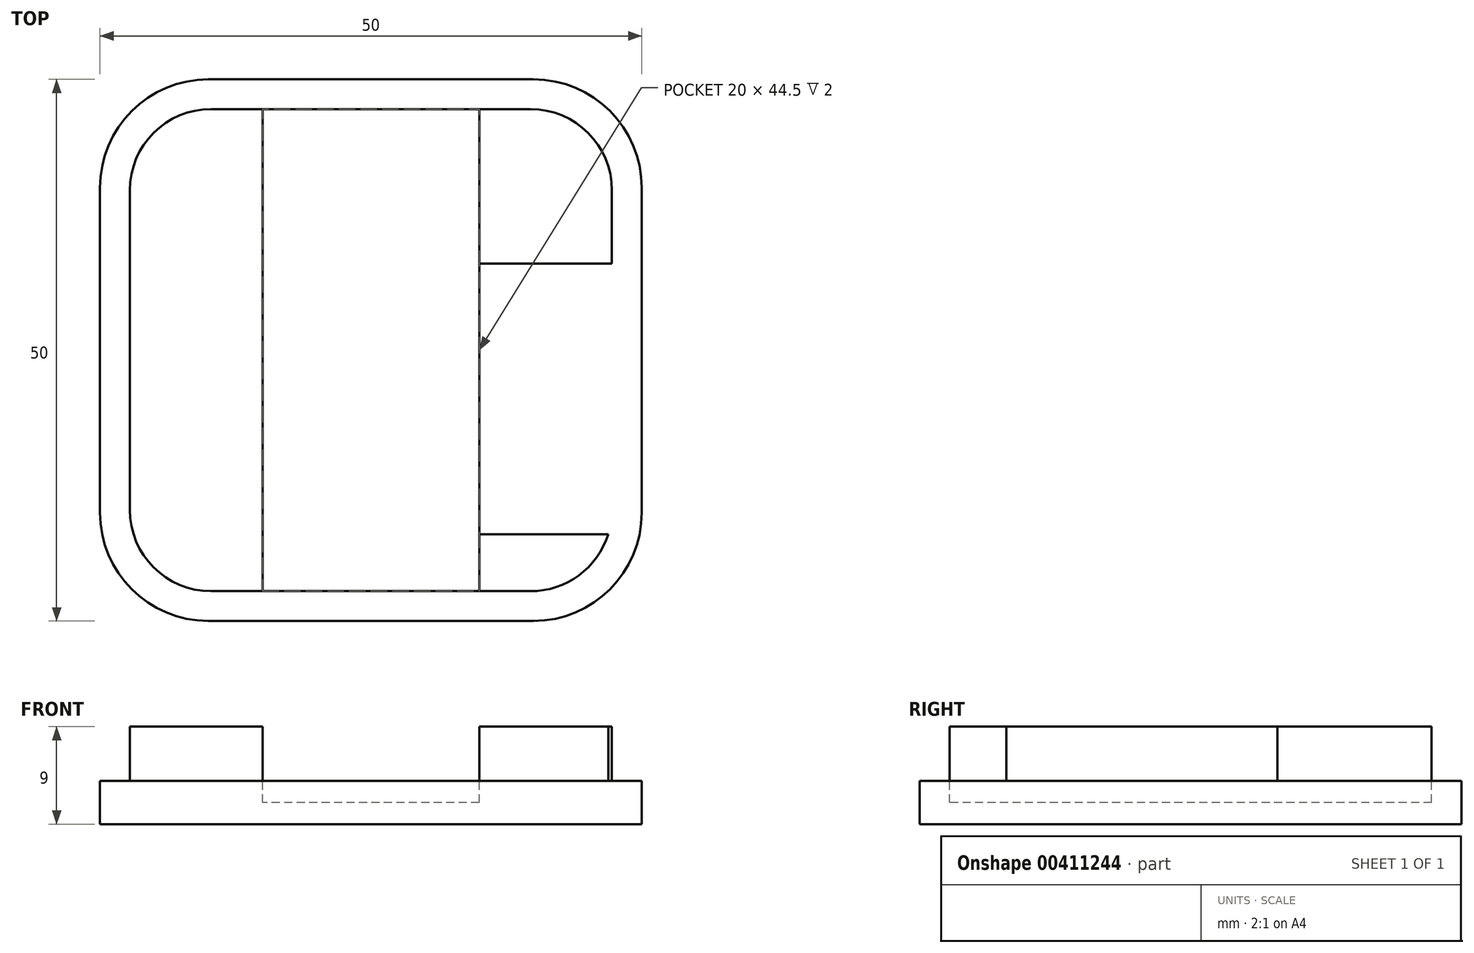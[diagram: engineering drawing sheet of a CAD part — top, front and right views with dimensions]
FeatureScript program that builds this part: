
annotation { "Feature Type Name" : "Feature", "Feature Type Description" : "" }
export const myFeature = defineFeature(function(context is Context, id is Id, definition is map)
    precondition{}
    {
        {
            var Q0;
            Q0=qCreatedBy(makeId("Top.planeOp"),FACE);
            var sketch = newSketch(context, id + "F0", { "sketchPlane" : qUnion([Q0])});
            skLineSegment(sketch, "E0.bottom", {"start": v(15, 25) * mm, "end": v(-15, 25) * mm});
            skLineSegment(sketch, "E0.top", {"start": v(15, -25) * mm, "end": v(-15, -25) * mm});
            skLineSegment(sketch, "E0.left", {"start": v(25, 15) * mm, "end": v(25, -15) * mm});
            skLineSegment(sketch, "E0.right", {"start": v(-25, 15) * mm, "end": v(-25, -15) * mm});
            skPoint(sketch, "E0.middle", {"position": v(0, 0) * mm});
            skPoint(sketch, "E1.visualSharp", {"position": v(-25, 25) * mm});
            skArc(sketch, "E1.filletArc", {"start": v(-15, 25) * mm, "mid": v(-22.07, 22.07) * mm, "end": v(-25, 15) * mm});
            skPoint(sketch, "E2.visualSharp", {"position": v(25, 25) * mm});
            skArc(sketch, "E2.filletArc", {"start": v(25, 15) * mm, "mid": v(22.07, 22.07) * mm, "end": v(15, 25) * mm});
            skPoint(sketch, "E3.visualSharp", {"position": v(25, -25) * mm});
            skArc(sketch, "E3.filletArc", {"start": v(15, -25) * mm, "mid": v(22.07, -22.07) * mm, "end": v(25, -15) * mm});
            skPoint(sketch, "E4.visualSharp", {"position": v(-25, -25) * mm});
            skArc(sketch, "E4.filletArc", {"start": v(-25, -15) * mm, "mid": v(-22.07, -22.07) * mm, "end": v(-15, -25) * mm});
            skSolve(sketch);
        }
        {
            var Q0;
            Q0=makeQuery(id+"F0.imprint","IMPRINT",FACE,{"disambiguationData":[TD([[makeQuery(id+"F0.imprint","IMPRINT",EDGE,{"derivedFrom":sQuery(id+"F0.wireOp",EDGE,"E0.bottom")}),1.0]])]});
            extrude(context, id + "F1", {"entities" : qUnion([Q0]), "depth" : 4 * mm});
        }
        {
            var Q0;
            Q0=makeQuery(id+"F1.opExtrude","CAP_FACE",FACE,{"disambiguationData":[OSD([sQuery(id+"F0.wireOp",EDGE,"E0.bottom"),sQuery(id+"F0.wireOp",EDGE,"E0.top"),sQuery(id+"F0.wireOp",EDGE,"E0.left"),sQuery(id+"F0.wireOp",EDGE,"E0.right"),sQuery(id+"F0.wireOp",EDGE,"E1.filletArc"),sQuery(id+"F0.wireOp",EDGE,"E2.filletArc"),sQuery(id+"F0.wireOp",EDGE,"E3.filletArc"),sQuery(id+"F0.wireOp",EDGE,"E4.filletArc")])],"isStart":false});
            var sketch = newSketch(context, id + "F2", { "sketchPlane" : qUnion([Q0])});
            skLineSegment(sketch, "E5.bottom", {"start": v(14.75, 22.25) * mm, "end": v(-14.75, 22.25) * mm});
            skLineSegment(sketch, "E5.top", {"start": v(14.75, -22.25) * mm, "end": v(-14.75, -22.25) * mm});
            skLineSegment(sketch, "E5.left", {"start": v(22.25, 14.75) * mm, "end": v(22.25, -14.75) * mm});
            skLineSegment(sketch, "E5.right", {"start": v(-22.25, 14.75) * mm, "end": v(-22.25, -14.75) * mm});
            skPoint(sketch, "E5.middle", {"position": v(0, 0) * mm});
            skPoint(sketch, "E6.visualSharp", {"position": v(-22.25, 22.25) * mm});
            skArc(sketch, "E6.filletArc", {"start": v(-14.75, 22.25) * mm, "mid": v(-20.05, 20.05) * mm, "end": v(-22.25, 14.75) * mm});
            skPoint(sketch, "E7.visualSharp", {"position": v(22.25, 22.25) * mm});
            skArc(sketch, "E7.filletArc", {"start": v(22.25, 14.75) * mm, "mid": v(20.05, 20.05) * mm, "end": v(14.75, 22.25) * mm});
            skPoint(sketch, "E8.visualSharp", {"position": v(22.25, -22.25) * mm});
            skArc(sketch, "E8.filletArc", {"start": v(14.75, -22.25) * mm, "mid": v(20.05, -20.05) * mm, "end": v(22.25, -14.75) * mm});
            skPoint(sketch, "E9.visualSharp", {"position": v(-22.25, -22.25) * mm});
            skArc(sketch, "E9.filletArc", {"start": v(-22.25, -14.75) * mm, "mid": v(-20.05, -20.05) * mm, "end": v(-14.75, -22.25) * mm});
            skSolve(sketch);
        }
        {
            var Q0;
            Q0=makeQuery(id+"F2.imprint","IMPRINT",FACE,{"disambiguationData":[TD([[makeQuery(id+"F2.imprint","IMPRINT",EDGE,{"derivedFrom":sQuery(id+"F2.wireOp",EDGE,"E5.bottom")}),1.0]])]});
            extrude(context, id + "F3", {"entities" : qUnion([Q0]), "operationType" : NewBodyOperationType.ADD, "depth" : 5 * mm});
        }
        {
            var Q0;
            Q0=makeQuery(id+"F3.opExtrude","CAP_FACE",FACE,{"disambiguationData":[OSD([sQuery(id+"F2.wireOp",EDGE,"E5.bottom"),sQuery(id+"F2.wireOp",EDGE,"E5.top"),sQuery(id+"F2.wireOp",EDGE,"E5.left"),sQuery(id+"F2.wireOp",EDGE,"E5.right"),sQuery(id+"F2.wireOp",EDGE,"E6.filletArc"),sQuery(id+"F2.wireOp",EDGE,"E7.filletArc"),sQuery(id+"F2.wireOp",EDGE,"E8.filletArc"),sQuery(id+"F2.wireOp",EDGE,"E9.filletArc")])],"isStart":false});
            var sketch = newSketch(context, id + "F4", { "sketchPlane" : qUnion([Q0])});
            skLineSegment(sketch, "E10.bottom", {"start": v(10, 22.25) * mm, "end": v(-10, 22.25) * mm});
            skLineSegment(sketch, "E10.top", {"start": v(10, -22.25) * mm, "end": v(-10, -22.25) * mm});
            skLineSegment(sketch, "E10.left", {"start": v(10, 22.25) * mm, "end": v(10, -22.25) * mm});
            skLineSegment(sketch, "E10.right", {"start": v(-10, 22.25) * mm, "end": v(-10, -22.25) * mm});
            skPoint(sketch, "E10.middle", {"position": v(0, 0) * mm});
            skSolve(sketch);
        }
        {
            var Q0;
            {var subQ0=sQuery(id+"F4.wireOp",EDGE,"E10.bottom");Q0=makeQuery(id+"F4.imprint","IMPRINT",FACE,{"disambiguationData":[TD([[makeQuery(id+"F4.imprint","IMPRINT",EDGE,{"derivedFrom":subQ0}),1.0]])]});}
            extrude(context, id + "F5", {"entities" : qUnion([Q0]), "operationType" : NewBodyOperationType.REMOVE, "oppositeDirection" : true, "depth" : 7 * mm});
        }
        {
            var Q0;
            Q0=makeQuery(id+"F3.opExtrude","SWEPT_FACE",FACE,{"disambiguationData":[OSD([sQuery(id+"F2.wireOp",EDGE,"E5.left")])]});
            var sketch = newSketch(context, id + "F6", { "sketchPlane" : qUnion([Q0])});
            skLineSegment(sketch, "E11.bottom", {"start": v(8, 9) * mm, "end": v(-17, 9) * mm});
            skLineSegment(sketch, "E11.top", {"start": v(8, 4) * mm, "end": v(-17, 4) * mm});
            skLineSegment(sketch, "E11.left", {"start": v(8, 9) * mm, "end": v(8, 4) * mm});
            skLineSegment(sketch, "E11.right", {"start": v(-17, 9) * mm, "end": v(-17, 4) * mm});
            skSolve(sketch);
        }
        {
            var Q0;
            Q0 = qSketchRegion(id + "F6", true);
            extrude(context, id + "F7", {"entities" : qUnion([Q0]), "operationType" : NewBodyOperationType.REMOVE, "oppositeDirection" : true, "depth" : 13 * mm});
        }
    });
